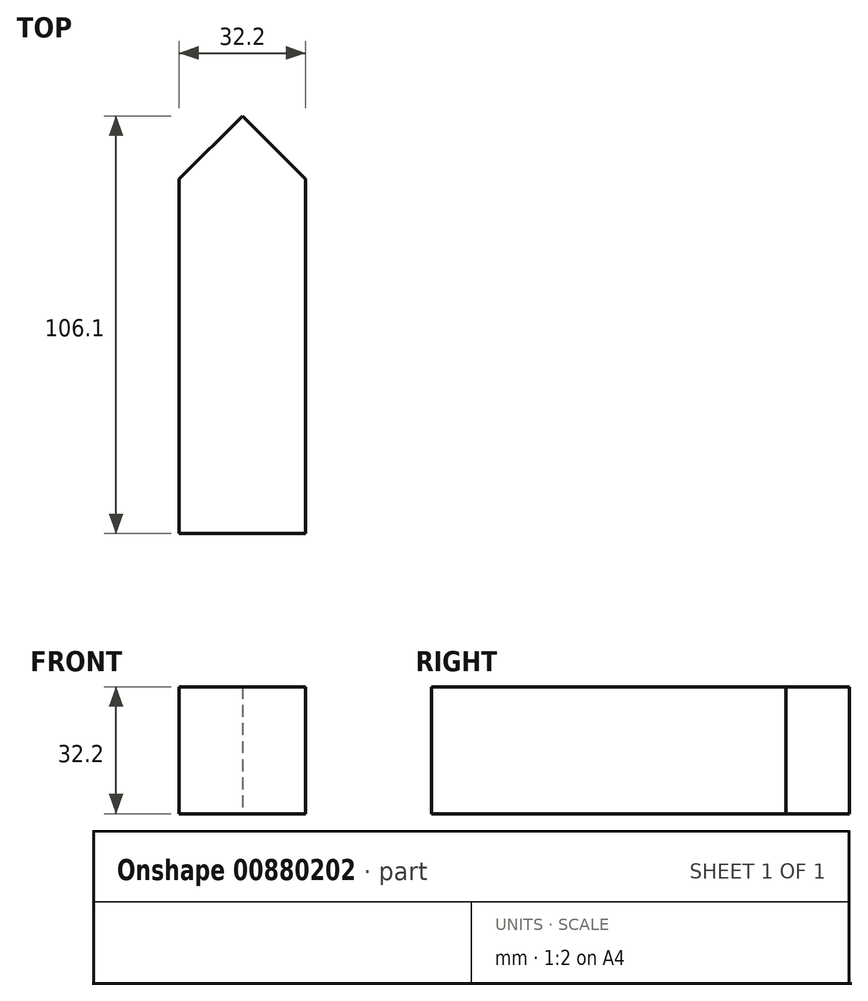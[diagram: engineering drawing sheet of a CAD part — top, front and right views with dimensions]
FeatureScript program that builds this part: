
annotation { "Feature Type Name" : "Feature", "Feature Type Description" : "" }
export const myFeature = defineFeature(function(context is Context, id is Id, definition is map)
    precondition{}
    {
        {
            var Q0;
            Q0=qCreatedBy(makeId("Top.planeOp"),FACE);
            var sketch = newSketch(context, id + "F0", { "sketchPlane" : qUnion([Q0])});
            skLineSegment(sketch, "E0.bottom", {"start": v(16.1, -45) * mm, "end": v(-16.1, -45) * mm});
            skLineSegment(sketch, "E0.left", {"start": v(16.1, -45) * mm, "end": v(16.1, 45) * mm});
            skLineSegment(sketch, "E0.right", {"start": v(-16.1, -45) * mm, "end": v(-16.1, 45) * mm});
            skPoint(sketch, "E0.middle", {"position": v(0, 0) * mm});
            skLineSegment(sketch, "E1", {"start": v(-16.1, 45) * mm, "end": v(0, 61.1) * mm});
            skLineSegment(sketch, "E2", {"start": v(0, 61.1) * mm, "end": v(16.1, 45) * mm});
            skSolve(sketch);
        }
        {
            var Q0;
            Q0=makeQuery(id+"F0.imprint","IMPRINT",FACE,{"disambiguationData":[TD([[makeQuery(id+"F0.imprint","IMPRINT",EDGE,{"derivedFrom":sQuery(id+"F0.wireOp",EDGE,"E0.bottom")}),-1.0]])]});
            extrude(context, id + "F1", {"entities" : qUnion([Q0]), "depth" : 32.2 * mm, "offsetDistance" : 25 * mm});
        }
    });
